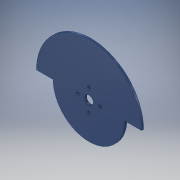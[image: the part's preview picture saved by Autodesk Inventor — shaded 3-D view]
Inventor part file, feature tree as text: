
AUTODESK INVENTOR PART (.ipt)
format: ipt  version: 2017 (Build 210142000, 142)  size: 124,416 bytes
history: native  units: in
note: dims shown in document units (in); Inventor stores cm internally (conversion verified against a paired STEP export)
features: extrude x1, sketch x1
ambient origin geometry x8: Origin, YZ Plane, XZ Plane, XY Plane, X Axis, Y Axis, Z Axis, Center Point
bodies: Solid1 (feature_tree)
feature tree (2):
  extrude  "Extrusion1"  Depth=0.0625in
  sketch  "Sketch1"  dims[d0=0.28in d1=0.1in d2=0.36in d3=1.5748in d5=360.0deg d7=1.7in d8=1.16in d9=1.4in d10=1.37in d11=1.37in d12=0.87in d13=0.01in d14=0.29in d15=0.0625in d16=0.0in]
